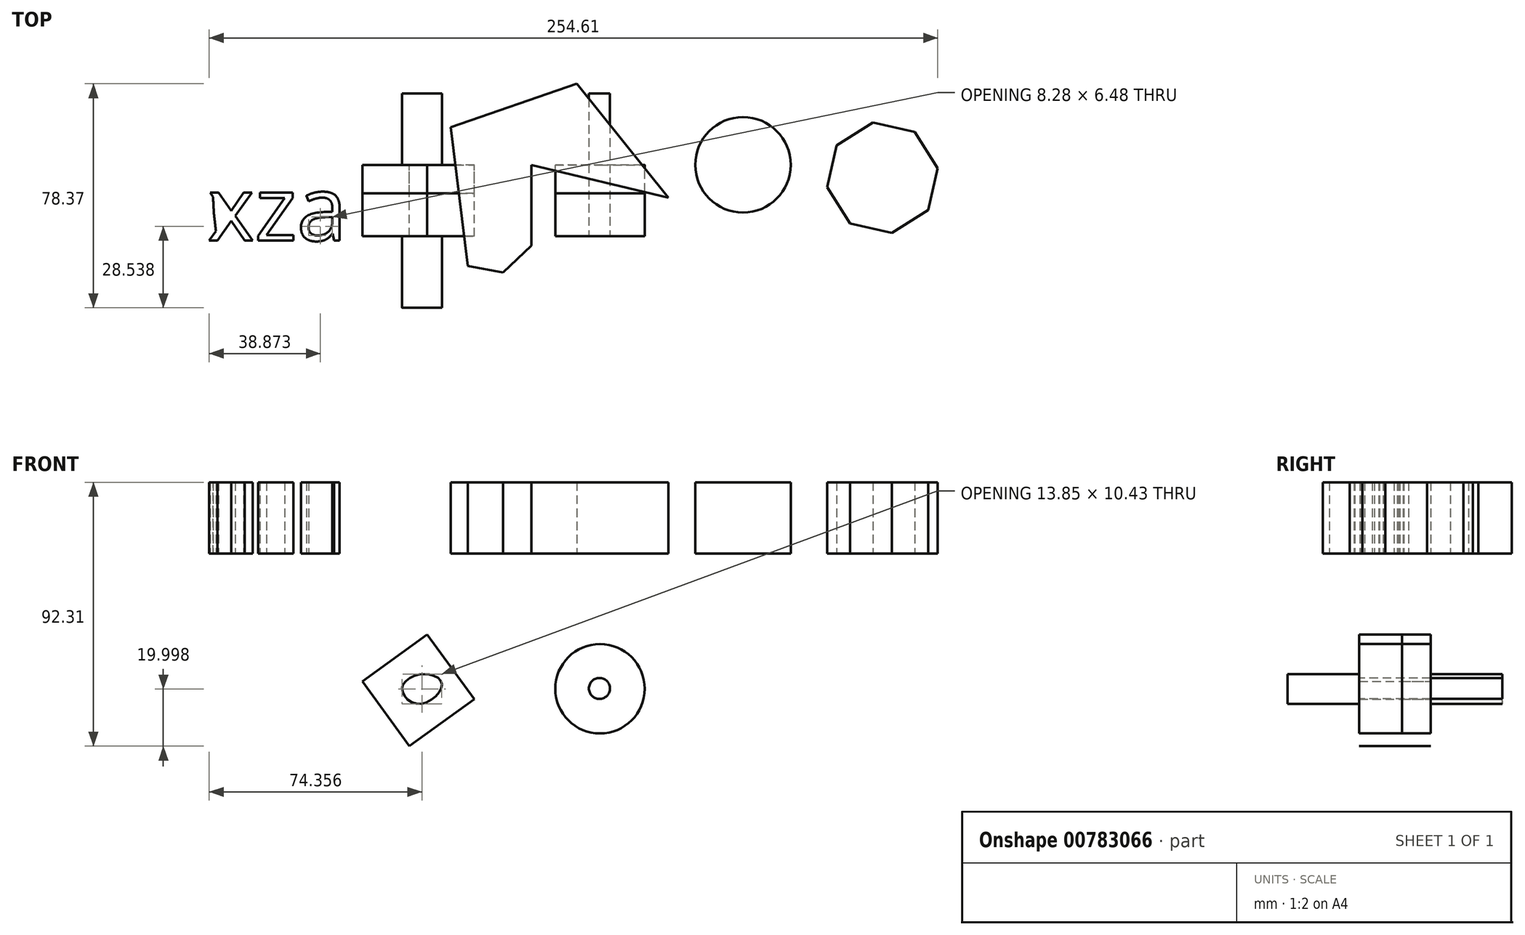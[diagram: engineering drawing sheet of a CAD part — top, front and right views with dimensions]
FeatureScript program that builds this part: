
annotation { "Feature Type Name" : "Feature", "Feature Type Description" : "" }
export const myFeature = defineFeature(function(context is Context, id is Id, definition is map)
    precondition{}
    {
        {
            var Q0;
            Q0=qCreatedBy(makeId("Top.planeOp"),FACE);
            var sketch = newSketch(context, id + "F0", { "sketchPlane" : qUnion([Q0])});
            skLineSegment(sketch, "E0", {"start": v(-38.08, -35.38) * mm, "end": v(-44.05, 13.18) * mm});
            skLineSegment(sketch, "E1", {"start": v(-44.05, 13.18) * mm, "end": v(0, 28.37) * mm});
            skLineSegment(sketch, "E2", {"start": v(0, 28.37) * mm, "end": v(32.03, -11.45) * mm});
            skLineSegment(sketch, "E3", {"start": v(32.03, -11.45) * mm, "end": v(-15.9, 0) * mm});
            skLineSegment(sketch, "E4", {"start": v(-15.9, 0) * mm, "end": v(-15.9, -28.27) * mm});
            skLineSegment(sketch, "E5", {"start": v(-15.9, -28.27) * mm, "end": v(-25.71, -37.7) * mm});
            skLineSegment(sketch, "E6", {"start": v(-25.71, -37.7) * mm, "end": v(-38.08, -35.38) * mm});
            skCircle(sketch, "E7", {"center": v(58.1, 0) * mm, "radius": 16.69 * mm});
            skArc(sketch, "E8", {"start": v(113.7, 38.85) * mm, "mid": v(105.2, 52.87) * mm, "end": v(89.23, 49.15) * mm});
            skCircle(sketch, "E9.cCircle", {"center": v(106.82, -4.52) * mm, "radius": 18.1 * mm, "construction": true});
            skLineSegment(sketch, "E9.0", {"start": v(118.15, 11.46) * mm, "end": v(126.14, -1.23) * mm});
            skLineSegment(sketch, "E9.1", {"start": v(126.14, -1.23) * mm, "end": v(122.8, -15.85) * mm});
            skLineSegment(sketch, "E9.2", {"start": v(122.8, -15.85) * mm, "end": v(110.11, -23.83) * mm});
            skLineSegment(sketch, "E9.3", {"start": v(110.11, -23.83) * mm, "end": v(95.5, -20.5) * mm});
            skLineSegment(sketch, "E9.4", {"start": v(95.5, -20.5) * mm, "end": v(87.51, -7.8) * mm});
            skLineSegment(sketch, "E9.5", {"start": v(87.51, -7.8) * mm, "end": v(90.84, 6.81) * mm});
            skLineSegment(sketch, "E9.6", {"start": v(90.84, 6.81) * mm, "end": v(103.54, 14.8) * mm});
            skLineSegment(sketch, "E9.7", {"start": v(103.54, 14.8) * mm, "end": v(118.15, 11.46) * mm});
            skPoint(sketch, "E9.0.midPoint", {"position": v(122.14, 5.11) * mm});
            skPoint(sketch, "E10", {"position": v(21.24, -50.78) * mm});
            skFitSpline(sketch, "E11", {"points": [v(-123.52, -38.22) * mm, v(-121.49, 0) * mm, v(-84.13, -6.8) * mm, v(-82.32, 34.42) * mm, v(-82.37, 35.19) * mm], "startDerivative": vector(-32.05, 174.38) * mm, "endDerivative": vector(1.14, 6.33) * mm});
            skText(sketch, "E12", { "text": "\nxza\n", "fontName": "OpenSans-Regular.ttf"});
            skLineSegment(sketch, "E13", {"start": v(-51.42, -62.78) * mm, "end": v(12.22, -62.78) * mm, "construction": true});
            const initialGuessF0  = {"E12": [-0.12907, 0.0163, 1, 0, 0.02266]};
            skSetInitialGuess(sketch, initialGuessF0);
            skSolve(sketch);
        }
        {
            var Q0;
            Q0 = qSketchRegion(id + "F0", true);
            extrude(context, id + "F1", {"entities" : qUnion([Q0]), "depth" : 25 * mm, "offsetDistance" : 25 * mm});
        }
        {
            var Q0;
            Q0=qCreatedBy(makeId("Front.planeOp"),FACE);
            cPlane(context, id + "F2", {"entities" : qUnion([Q0]), "cplaneType" : CPlaneType.OFFSET, "offset" : 100 * mm, "oppositeDirection" : true, "width" : 150 * mm, "height" : 150 * mm});
        }
        {
            var Q0;
            Q0=qCreatedBy(makeId("Front.planeOp"),FACE);
            var sketch = newSketch(context, id + "F3", { "sketchPlane" : qUnion([Q0])});
            skCircle(sketch, "E14", {"center": v(8.1, -47.25) * mm, "radius": 15.63 * mm});
            skCircle(sketch, "E15.cCircle", {"center": v(-55.38, -47.76) * mm, "radius": 14 * mm, "construction": true});
            skLineSegment(sketch, "E15.0", {"start": v(-35.83, -50.87) * mm, "end": v(-58.49, -67.31) * mm});
            skLineSegment(sketch, "E15.1", {"start": v(-58.49, -67.31) * mm, "end": v(-74.93, -44.66) * mm});
            skLineSegment(sketch, "E15.2", {"start": v(-74.93, -44.66) * mm, "end": v(-52.27, -28.21) * mm});
            skLineSegment(sketch, "E15.3", {"start": v(-52.27, -28.21) * mm, "end": v(-35.83, -50.87) * mm});
            skPoint(sketch, "E15.0.midPoint", {"position": v(-47.16, -59.1) * mm});
            skSolve(sketch);
        }
        {
            var Q0;
            Q0 = qSketchRegion(id + "F3", true);
            var Q1;
            Q1=makeQuery(id+"F3.imprint","IMPRINT",FACE,{"disambiguationData":[TD([[makeQuery(id+"F3.imprint","IMPRINT",EDGE,{"derivedFrom":sQuery(id+"F3.wireOp",EDGE,"E14")}),1.0]])]});
            extrude(context, id + "F4", {"entities" : qUnion([Q0, Q1]), "depth" : 25 * mm, "offsetDistance" : 25 * mm});
        }
        {
            var Q0;
            Q0 = qSketchRegion(id + "F3", true);
            extrude(context, id + "F5", {"entities" : qUnion([Q0]), "depth" : 10 * mm, "offsetDistance" : 25 * mm});
        }
        {
            var Q0;
            Q0=makeQuery(id+"F4.opExtrude","CAP_FACE",FACE,{"disambiguationData":[OSD([sQuery(id+"F3.wireOp",EDGE,"E15.0"),sQuery(id+"F3.wireOp",EDGE,"E15.1"),sQuery(id+"F3.wireOp",EDGE,"E15.2"),sQuery(id+"F3.wireOp",EDGE,"E15.3")])],"isStart":false});
            var sketch = newSketch(context, id + "F6", { "sketchPlane" : qUnion([Q0])});
            skPoint(sketch, "E16.2.internal.snap0", {"position": v(-47.16, -59.1) * mm});
            skFitSpline(sketch, "E16", {"points": [v(-61.04, -46.94) * mm, v(-55.1, -52.54) * mm, v(-47.16, -45.8) * mm, v(-53.73, -42.1) * mm, v(-61.04, -46.94) * mm]});
            skCircle(sketch, "E17", {"center": v(7.92, -47.13) * mm, "radius": 3.68 * mm});
            skSolve(sketch);
        }
        {
            var Q0;
            Q0 = qSketchRegion(id + "F6", true);
            extrude(context, id + "F7", {"entities" : qUnion([Q0]), "oppositeDirection" : true, "depth" : 50 * mm, "offsetDistance" : 25 * mm});
        }
        {
            var Q0;
            Q0=makeQuery(id+"F7.opExtrude","CAP_FACE",FACE,{"disambiguationData":[OSD([sQuery(id+"F6.wireOp",EDGE,"E16")])],"isStart":true});
            extrude(context, id + "F8", {"entities" : qUnion([Q0]), "operationType" : NewBodyOperationType.ADD, "depth" : 25 * mm, "offsetDistance" : 25 * mm});
        }
    });
